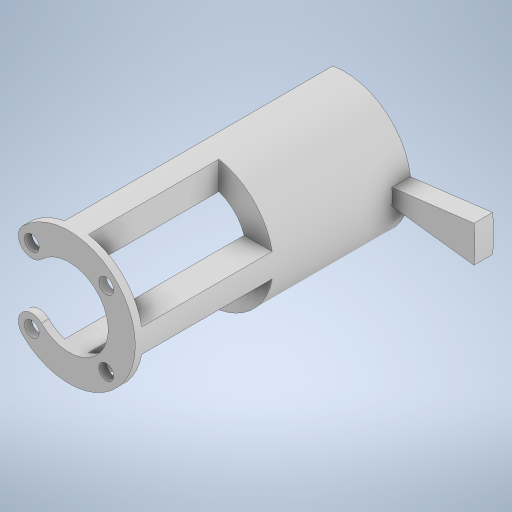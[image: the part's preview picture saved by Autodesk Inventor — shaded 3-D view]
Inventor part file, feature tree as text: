
AUTODESK INVENTOR PART (.ipt)
format: ipt  version: 2024 (Build 280153000, 153)  size: 346,112 bytes
history: native  units: mm
features: projected_geometry x8, extrude x5, sketch x4
ambient origin geometry x8: Origin, YZ Plane, XZ Plane, XY Plane, X Axis, Y Axis, Z Axis, Center Point
bodies: Solid1 (feature_tree)
feature tree (17):
  extrude  "Extrusion1"  Depth=2.0mm TaperAngle=0.0deg
  extrude  "Extrusion2"  Depth=10.0mm TaperAngle=0.0deg
  extrude  "Extrusion3"  Depth=40.0mm
  extrude  "Extrusion4"  Depth=5.0mm TaperAngle=0.0deg
  extrude  "Extrusion5"  [1 undecoded]
  sketch  "Sketch1"  dims[d0=21.0mm d1=2.0mm d2=0.0mm]
  sketch  "Sketch2"  dims[d3=10.0mm d4=0.0mm d5=62.0mm d6=0.0mm]
  projected_geometry  "Projected Loop1"
  projected_geometry  "Projected Loop7"
  projected_geometry  "Projected Loop8"
  projected_geometry  "Projected Loop9"
  projected_geometry  "Projected Loop10"
  projected_geometry  "Projected Loop11"
  sketch  "Sketch5"  dims[d7=40.0mm d8=1.22173mm]
  sketch  "Sketch6"  dims[d9=5.0mm d10=0.0mm d11=25.0mm d12=0.0mm]
  projected_geometry  "Projected Loop12"
  projected_geometry  "Projected Loop13"
note: 1 required parameter value undecoded (feature->parameter linkage not recoverable at this tier; creation-order binding heuristic only, values carry confidence <= 0.55)
